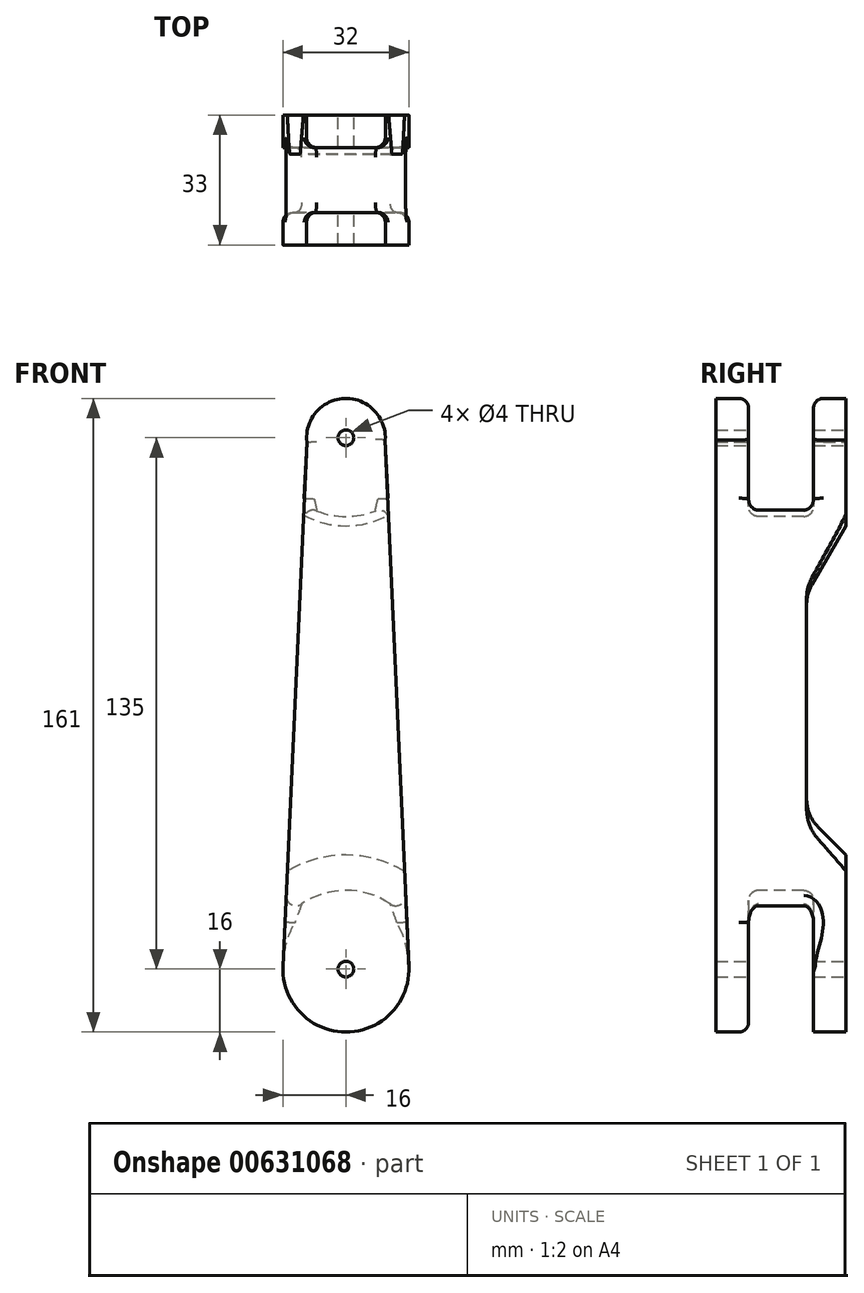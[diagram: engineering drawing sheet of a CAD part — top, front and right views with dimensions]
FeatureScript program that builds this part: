
annotation { "Feature Type Name" : "Feature", "Feature Type Description" : "" }
export const myFeature = defineFeature(function(context is Context, id is Id, definition is map)
    precondition{}
    {
        {
            var Q0;
            Q0=qCreatedBy(makeId("Front.planeOp"),FACE);
            var sketch = newSketch(context, id + "F0", { "sketchPlane" : qUnion([Q0])});
            skLineSegment(sketch, "E0", {"start": v(0, 0) * mm, "end": v(0, 135) * mm, "construction": true});
            skCircle(sketch, "E1", {"center": v(0, 135) * mm, "radius": 10 * mm});
            skCircle(sketch, "E2", {"center": v(0, 0) * mm, "radius": 16 * mm});
            skLineSegment(sketch, "E3", {"start": v(9.99, 134.48) * mm, "end": v(16.02, 0) * mm});
            skLineSegment(sketch, "E4", {"start": v(-9.94, 133.94) * mm, "end": v(-16.02, 0) * mm});
            skSolve(sketch);
        }
        {
            var Q0;
            Q0=qSketchRegion(id+"F0",true);
            extrude(context, id + "F1", {"entities" : qUnion([Q0]), "endBound" : BoundingType.SYMMETRIC, "depth" : 33 * mm});
        }
        {
            var Q0;
            Q0=qCreatedBy(makeId("Front.planeOp"),FACE);
            var sketch = newSketch(context, id + "F2", { "sketchPlane" : qUnion([Q0])});
            skCircle(sketch, "E5", {"center": v(0, 135) * mm, "radius": 20 * mm});
            skCircle(sketch, "E6", {"center": v(0, 0) * mm, "radius": 20 * mm});
            skSolve(sketch);
        }
        {
            var Q0;
            Q0 = qSketchRegion(id + "F2", true);
            extrude(context, id + "F3", {"entities" : qUnion([Q0]), "operationType" : NewBodyOperationType.REMOVE, "endBound" : BoundingType.SYMMETRIC, "oppositeDirection" : true, "depth" : 16.5 * mm, "offsetDistance" : 25 * mm});
        }
        {
            var Q0;
            Q0=qCreatedBy(makeId("Front.planeOp"),FACE);
            var sketch = newSketch(context, id + "F4", { "sketchPlane" : qUnion([Q0])});
            skCircle(sketch, "E7", {"center": v(0, 0) * mm, "radius": 2 * mm});
            skCircle(sketch, "E8", {"center": v(0, 135) * mm, "radius": 2 * mm});
            skSolve(sketch);
        }
        {
            var Q0;
            Q0=qCreatedBy(makeId("Right.planeOp"),FACE);
            var sketch = newSketch(context, id + "F5", { "sketchPlane" : qUnion([Q0])});
            skLineSegment(sketch, "E9", {"start": v(6.5, 70) * mm, "end": v(16.5, 70) * mm});
            skLineSegment(sketch, "E10", {"start": v(16.5, 70) * mm, "end": v(16.5, 29) * mm});
            skLineSegment(sketch, "E11", {"start": v(16.5, 29) * mm, "end": v(6.5, 39) * mm});
            skLineSegment(sketch, "E12", {"start": v(6.5, 39) * mm, "end": v(6.5, 70) * mm});
            skLineSegment(sketch, "E13", {"start": v(0, 0) * mm, "end": v(29.1, 0) * mm, "construction": true});
            skSolve(sketch);
        }
        {
            var Q0;
            Q0=qSketchRegion(id+"F5",true);
            var Q1;
            Q1=sQuery(id+"F5.wireOp",EDGE,"E13");
            revolve(context, id + "F6", {"operationType" : NewBodyOperationType.REMOVE, "entities" : qUnion([Q0]), "axis" : qUnion([Q1]), "revolveType" : RevolveType.FULL, "oppositeDirection" : true});
        }
        {
            var Q0;
            Q0=qCreatedBy(makeId("Right.planeOp"),FACE);
            var sketch = newSketch(context, id + "F7", { "sketchPlane" : qUnion([Q0])});
            skLineSegment(sketch, "E14", {"start": v(6.5, 56.25) * mm, "end": v(6.5, 95.28) * mm});
            skLineSegment(sketch, "E15", {"start": v(6.5, 95.28) * mm, "end": v(16.5, 112.6) * mm});
            skLineSegment(sketch, "E16", {"start": v(16.5, 112.6) * mm, "end": v(16.5, 56.25) * mm});
            skLineSegment(sketch, "E17", {"start": v(16.5, 56.25) * mm, "end": v(6.5, 56.25) * mm});
            skLineSegment(sketch, "E18", {"start": v(-22.24, 135) * mm, "end": v(31.2, 135) * mm, "construction": true});
            skSolve(sketch);
        }
        {
            var Q0;
            Q0 = qSketchRegion(id + "F7", true);
            var Q1;
            Q1=sQuery(id+"F7.wireOp",EDGE,"E18");
            revolve(context, id + "F8", {"operationType" : NewBodyOperationType.REMOVE, "entities" : qUnion([Q0]), "axis" : qUnion([Q1]), "revolveType" : RevolveType.FULL, "oppositeDirection" : true});
        }
        {
            var Q0;
            Q0=makeQuery(id+"F6.boolean.opBoolean","COPY",EDGE,{"derivedFrom":makeQuery(id+"F6.opRevolve","SWEPT_EDGE",EDGE,{"disambiguationData":[OSD([sQuery(id+"F5.wireOp",EDGE,"E11"),sQuery(id+"F5.wireOp",EDGE,"E12")])]})});
            var Q1;
            Q1=makeQuery(id+"F6.boolean.opBoolean","COPY",EDGE,{"derivedFrom":makeQuery(id+"F6.opRevolve","SWEPT_EDGE",EDGE,{"disambiguationData":[OSD([sQuery(id+"F5.wireOp",EDGE,"E10"),sQuery(id+"F5.wireOp",EDGE,"E11")])]})});
            var Q2;
            Q2=makeQuery(id+"F4pFOms0JvAV94v_1.boolean.opBoolean","COPY",EDGE,{"derivedFrom":makeQuery(id+"F4pFOms0JvAV94v_1.opRevolve","SWEPT_EDGE",EDGE,{"disambiguationData":[OSD([sQuery(id+"F7.wireOp",EDGE,"E14"),sQuery(id+"F7.wireOp",EDGE,"E15")])]})});
            var Q3;
            Q3=makeQuery(id+"F4pFOms0JvAV94v_1.boolean.opBoolean","COPY",EDGE,{"derivedFrom":makeQuery(id+"F4pFOms0JvAV94v_1.opRevolve","SWEPT_EDGE",EDGE,{"disambiguationData":[OSD([sQuery(id+"F7.wireOp",EDGE,"E15"),sQuery(id+"F7.wireOp",EDGE,"E16")])]})});
            fillet(context, id + "F9", {"entities" : qUnion([Q0, Q1, Q2, Q3]), "radius" : 10 * mm, "tangentPropagation" : true, "allowEdgeOverflow" : false});
        }
        {
            var Q0;
            Q0 = qSketchRegion(id + "F4", true);
            extrude(context, id + "F10", {"entities" : qUnion([Q0]), "operationType" : NewBodyOperationType.REMOVE, "endBound" : BoundingType.SYMMETRIC, "depth" : 70 * mm, "offsetDistance" : 25 * mm});
        }
        {
            var Q0;
            Q0=makeQuery(id+"F8.boolean.opBoolean","COPY",EDGE,{"derivedFrom":makeQuery(id+"F8.opRevolve","SWEPT_EDGE",EDGE,{"disambiguationData":[OSD([sQuery(id+"F7.wireOp",EDGE,"E14"),sQuery(id+"F7.wireOp",EDGE,"E15")])]})});
            var Q1;
            Q1=makeQuery(id+"F8.boolean.opBoolean","COPY",EDGE,{"derivedFrom":makeQuery(id+"F8.opRevolve","SWEPT_EDGE",EDGE,{"disambiguationData":[OSD([sQuery(id+"F7.wireOp",EDGE,"E15"),sQuery(id+"F7.wireOp",EDGE,"E16")])]})});
            fillet(context, id + "F11", {"entities" : qUnion([Q0, Q1]), "radius" : 10 * mm, "tangentPropagation" : true, "allowEdgeOverflow" : false});
        }
        {
            var Q0;
            Q0=makeQuery(id+"F3.boolean.opBoolean","INTERSECT",EDGE,{"derivedFrom":[makeQuery(id+"F1.opExtrude","SWEPT_FACE",FACE,{"disambiguationData":[OSD([sQuery(id+"F0.wireOp",EDGE,"E1")])]}),makeQuery(id+"F3.opExtrude","CAP_FACE",FACE,{"disambiguationData":[OSD([sQuery(id+"F2.wireOp",EDGE,"E5")])],"isStart":true})]});
            var Q1;
            Q1=makeQuery(id+"F3.boolean.opBoolean","INTERSECT",EDGE,{"derivedFrom":[makeQuery(id+"F1.opExtrude","SWEPT_FACE",FACE,{"disambiguationData":[OSD([sQuery(id+"F0.wireOp",EDGE,"E4")])]}),makeQuery(id+"F3.opExtrude","CAP_FACE",FACE,{"disambiguationData":[OSD([sQuery(id+"F2.wireOp",EDGE,"E5")])],"isStart":true})]});
            var Q2;
            Q2=makeQuery(id+"F3.boolean.opBoolean","INTERSECT",EDGE,{"derivedFrom":[makeQuery(id+"F1.opExtrude","SWEPT_FACE",FACE,{"disambiguationData":[OSD([sQuery(id+"F0.wireOp",EDGE,"E3")])]}),makeQuery(id+"F3.opExtrude","CAP_FACE",FACE,{"disambiguationData":[OSD([sQuery(id+"F2.wireOp",EDGE,"E5")])],"isStart":true})]});
            var Q3;
            Q3=makeQuery(id+"F3.boolean.opBoolean","COPY",EDGE,{"derivedFrom":makeQuery(id+"F3.opExtrude","CAP_EDGE",EDGE,{"disambiguationData":[OSD([sQuery(id+"F2.wireOp",EDGE,"E5")])],"isStart":true})});
            var Q4;
            Q4=makeQuery(id+"F3.boolean.opBoolean","INTERSECT",EDGE,{"derivedFrom":[makeQuery(id+"F1.opExtrude","SWEPT_FACE",FACE,{"disambiguationData":[OSD([sQuery(id+"F0.wireOp",EDGE,"E4")])]}),makeQuery(id+"F3.opExtrude","SWEPT_FACE",FACE,{"disambiguationData":[OSD([sQuery(id+"F2.wireOp",EDGE,"E5")])]})]});
            var Q5;
            Q5=makeQuery(id+"F3.boolean.opBoolean","INTERSECT",EDGE,{"derivedFrom":[makeQuery(id+"F1.opExtrude","SWEPT_FACE",FACE,{"disambiguationData":[OSD([sQuery(id+"F0.wireOp",EDGE,"E4")])]}),makeQuery(id+"F3.opExtrude","CAP_FACE",FACE,{"disambiguationData":[OSD([sQuery(id+"F2.wireOp",EDGE,"E5")])],"isStart":false})]});
            var Q6;
            Q6=makeQuery(id+"F3.boolean.opBoolean","INTERSECT",EDGE,{"derivedFrom":[makeQuery(id+"F1.opExtrude","SWEPT_FACE",FACE,{"disambiguationData":[OSD([sQuery(id+"F0.wireOp",EDGE,"E1")])]}),makeQuery(id+"F3.opExtrude","CAP_FACE",FACE,{"disambiguationData":[OSD([sQuery(id+"F2.wireOp",EDGE,"E5")])],"isStart":false})]});
            var Q7;
            Q7=makeQuery(id+"F3.boolean.opBoolean","INTERSECT",EDGE,{"derivedFrom":[makeQuery(id+"F1.opExtrude","SWEPT_FACE",FACE,{"disambiguationData":[OSD([sQuery(id+"F0.wireOp",EDGE,"E3")])]}),makeQuery(id+"F3.opExtrude","SWEPT_FACE",FACE,{"disambiguationData":[OSD([sQuery(id+"F2.wireOp",EDGE,"E5")])]})]});
            var Q8;
            Q8=makeQuery(id+"F3.boolean.opBoolean","INTERSECT",EDGE,{"derivedFrom":[makeQuery(id+"F1.opExtrude","SWEPT_FACE",FACE,{"disambiguationData":[OSD([sQuery(id+"F0.wireOp",EDGE,"E3")])]}),makeQuery(id+"F3.opExtrude","CAP_FACE",FACE,{"disambiguationData":[OSD([sQuery(id+"F2.wireOp",EDGE,"E5")])],"isStart":false})]});
            var Q9;
            Q9=makeQuery(id+"F3.boolean.opBoolean","COPY",EDGE,{"derivedFrom":makeQuery(id+"F3.opExtrude","CAP_EDGE",EDGE,{"disambiguationData":[OSD([sQuery(id+"F2.wireOp",EDGE,"E5")])],"isStart":false})});
            fillet(context, id + "F12", {"entities" : qUnion([Q0, Q1, Q2, Q3, Q4, Q5, Q6, Q7, Q8, Q9]), "radius" : 2.5 * mm, "tangentPropagation" : true, "allowEdgeOverflow" : false});
        }
        {
            var Q0;
            Q0=makeQuery(id+"F3.boolean.opBoolean","INTERSECT",EDGE,{"derivedFrom":[makeQuery(id+"F1.opExtrude","SWEPT_FACE",FACE,{"disambiguationData":[OSD([sQuery(id+"F0.wireOp",EDGE,"E2")])]}),makeQuery(id+"F3.opExtrude","CAP_FACE",FACE,{"disambiguationData":[OSD([sQuery(id+"F2.wireOp",EDGE,"E6")])],"isStart":true})]});
            var Q1;
            Q1=makeQuery(id+"F3.boolean.opBoolean","INTERSECT",EDGE,{"derivedFrom":[makeQuery(id+"F1.opExtrude","SWEPT_FACE",FACE,{"disambiguationData":[OSD([sQuery(id+"F0.wireOp",EDGE,"E3")])]}),makeQuery(id+"F3.opExtrude","CAP_FACE",FACE,{"disambiguationData":[OSD([sQuery(id+"F2.wireOp",EDGE,"E6")])],"isStart":true})]});
            var Q2;
            Q2=makeQuery(id+"F3.boolean.opBoolean","COPY",FACE,{"derivedFrom":makeQuery(id+"F3.opExtrude","SWEPT_FACE",FACE,{"disambiguationData":[OSD([sQuery(id+"F2.wireOp",EDGE,"E6")])]})});
            fillet(context, id + "F13", {"entities" : qUnion([Q0, Q1, Q2]), "radius" : 2.5 * mm, "tangentPropagation" : true, "allowEdgeOverflow" : false});
        }
    });
